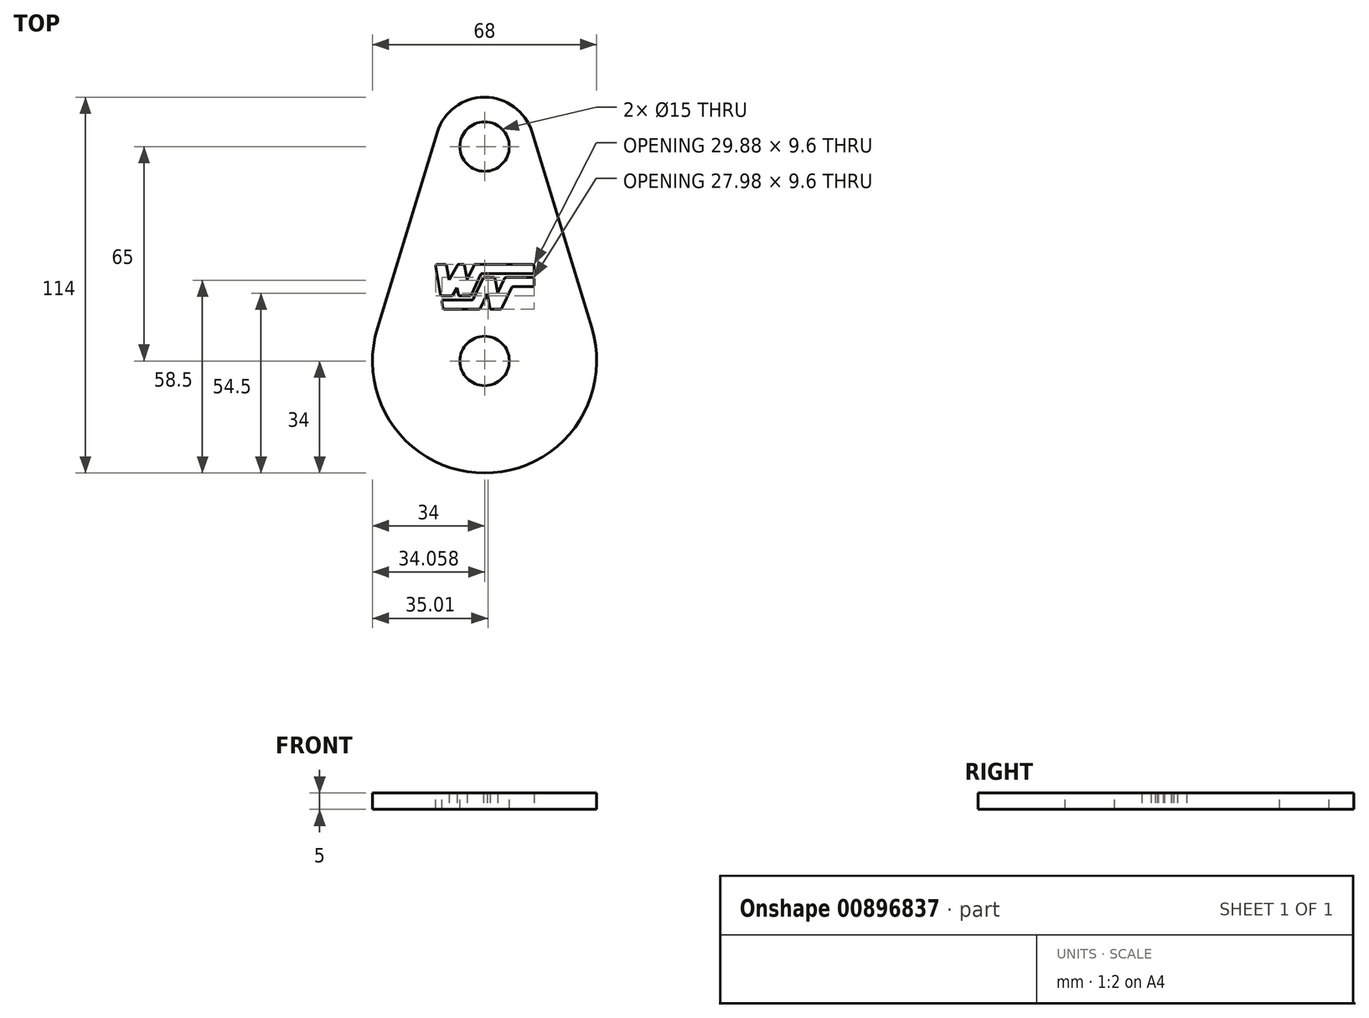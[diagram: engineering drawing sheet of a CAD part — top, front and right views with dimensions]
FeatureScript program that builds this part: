
annotation { "Feature Type Name" : "Feature", "Feature Type Description" : "" }
export const myFeature = defineFeature(function(context is Context, id is Id, definition is map)
    precondition{}
    {
        {
            var Q0;
            Q0=qCreatedBy(makeId("Top.planeOp"),FACE);
            var sketch = newSketch(context, id + "F0", { "sketchPlane" : qUnion([Q0])});
            skArc(sketch, "E0", {"start": v(14.34, 69.38) * mm, "mid": v(0, 80) * mm, "end": v(-14.34, 69.38) * mm});
            skArc(sketch, "E1", {"start": v(-32.52, 9.94) * mm, "mid": v(0, -34) * mm, "end": v(32.52, 9.94) * mm});
            skLineSegment(sketch, "E2", {"start": v(-32.52, 9.94) * mm, "end": v(-14.34, 69.38) * mm});
            skLineSegment(sketch, "E3", {"start": v(14.34, 69.38) * mm, "end": v(32.52, 9.94) * mm});
            skSolve(sketch);
        }
        {
            var Q0;
            Q0=makeQuery(id+"F0.imprint","IMPRINT",FACE,{"disambiguationData":[TD([[makeQuery(id+"F0.imprint","IMPRINT",EDGE,{"derivedFrom":sQuery(id+"F0.wireOp",EDGE,"E0")}),1.0]])]});
            extrude(context, id + "F1", {"entities" : qUnion([Q0]), "flatOperationType" : FlatOperationType.REMOVE, "depth" : 5 * mm, "offsetDistance" : 25 * mm, "domain" : OperationDomain.MODEL});
        }
        {
            var Q0;
            Q0=makeQuery(id+"F1.opExtrude","CAP_FACE",FACE,{"disambiguationData":[OSD([sQuery(id+"F0.wireOp",EDGE,"E0"),sQuery(id+"F0.wireOp",EDGE,"E1"),sQuery(id+"F0.wireOp",EDGE,"E2"),sQuery(id+"F0.wireOp",EDGE,"E3")])],"isStart":true});
            var sketch = newSketch(context, id + "F2", { "sketchPlane" : qUnion([Q0])});
            skPoint(sketch, "E4", {"position": v(0, -65) * mm});
            skPoint(sketch, "E5", {"position": v(0, 0) * mm});
            skSolve(sketch);
        }
        {
            var Q0;
            Q0=sQuery(id+"F2.wireOp",VERTEX,"E4");
            var Q1;
            Q1=sQuery(id+"F2.wireOp",VERTEX,"E5");
            var Q2;
            Q2=makeQuery(id+"F1.opExtrude","SWEPT_BODY",BODY,{"disambiguationData":[OSD([sQuery(id+"F0.wireOp",EDGE,"E0"),sQuery(id+"F0.wireOp",EDGE,"E1"),sQuery(id+"F0.wireOp",EDGE,"E2"),sQuery(id+"F0.wireOp",EDGE,"E3")])]});
            hole(context, id + "F3", {"style" : HoleStyle.SIMPLE, "endStyle" : HoleEndStyle.THROUGH, "holeDiameter" : 15 * mm, "majorDiameter" : 5 * mm, "isTappedThrough" : true, "tappedDepth" : 12 * mm, "tapClearance" : 3, "locations" : qUnion([Q0, Q1]), "scope" : qUnion([Q2])});
        }
        {
            var Q0;
            Q0=qCreatedBy(makeId("Top.planeOp"),FACE);
            var sketch = newSketch(context, id + "F4", { "sketchPlane" : qUnion([Q0])});
            skLineSegment(sketch, "E6.bottom", {"start": v(-15, 15) * mm, "end": v(-15, 30) * mm, "construction": true});
            skLineSegment(sketch, "E6.top", {"start": v(15, 15) * mm, "end": v(15, 30) * mm, "construction": true});
            skLineSegment(sketch, "E6.left", {"start": v(-15, 15) * mm, "end": v(15, 15) * mm, "construction": true});
            skLineSegment(sketch, "E6.right", {"start": v(-15, 30) * mm, "end": v(15, 30) * mm, "construction": true});
            skPoint(sketch, "E6.middle", {"position": v(0, 22.5) * mm});
            skLineSegment(sketch, "E7", {"start": v(15, 22.5) * mm, "end": v(-15, 22.5) * mm, "construction": true});
            skLineSegment(sketch, "E8", {"start": v(-15, 29.3) * mm, "end": v(-13.3, 19.7) * mm});
            skLineSegment(sketch, "E9", {"start": v(-13.3, 19.7) * mm, "end": v(-9.8, 19.7) * mm});
            skLineSegment(sketch, "E10", {"start": v(-9.8, 19.7) * mm, "end": v(-8.36, 22.2) * mm});
            skLineSegment(sketch, "E11", {"start": v(-8.36, 22.2) * mm, "end": v(-7.92, 19.7) * mm});
            skLineSegment(sketch, "E12", {"start": v(-7.92, 19.7) * mm, "end": v(-4.22, 19.7) * mm});
            skLineSegment(sketch, "E13", {"start": v(-4.22, 19.7) * mm, "end": v(-1.05, 26.5) * mm});
            skLineSegment(sketch, "E14", {"start": v(-1.05, 26.5) * mm, "end": v(15, 26.5) * mm});
            skLineSegment(sketch, "E15", {"start": v(15, 26.5) * mm, "end": v(15, 29.3) * mm});
            skLineSegment(sketch, "E16", {"start": v(15, 29.3) * mm, "end": v(-3.17, 29.3) * mm});
            skLineSegment(sketch, "E17", {"start": v(-3.17, 29.3) * mm, "end": v(-5.3, 24.73) * mm});
            skLineSegment(sketch, "E18", {"start": v(-5.3, 24.73) * mm, "end": v(-6.1, 29.3) * mm});
            skLineSegment(sketch, "E19", {"start": v(-6.1, 29.3) * mm, "end": v(-8.1, 29.3) * mm});
            skLineSegment(sketch, "E20", {"start": v(-8.1, 29.3) * mm, "end": v(-10.82, 24.6) * mm});
            skLineSegment(sketch, "E21", {"start": v(-10.82, 24.6) * mm, "end": v(-11.65, 29.3) * mm});
            skLineSegment(sketch, "E22", {"start": v(-11.65, 29.3) * mm, "end": v(-15, 29.3) * mm});
            skLineSegment(sketch, "E23", {"start": v(-13.1, 18.5) * mm, "end": v(-12.6, 15.7) * mm});
            skLineSegment(sketch, "E24", {"start": v(-12.6, 15.7) * mm, "end": v(-1.4, 15.7) * mm});
            skLineSegment(sketch, "E25", {"start": v(-1.4, 15.7) * mm, "end": v(0.79, 20.4) * mm});
            skLineSegment(sketch, "E26", {"start": v(0.79, 20.4) * mm, "end": v(1.62, 15.7) * mm});
            skLineSegment(sketch, "E27", {"start": v(1.62, 15.7) * mm, "end": v(5.12, 15.7) * mm});
            skLineSegment(sketch, "E28", {"start": v(5.12, 15.7) * mm, "end": v(8.29, 22.5) * mm});
            skLineSegment(sketch, "E29", {"start": v(8.29, 22.5) * mm, "end": v(15, 22.5) * mm});
            skLineSegment(sketch, "E30", {"start": v(15, 22.5) * mm, "end": v(15, 25.3) * mm});
            skLineSegment(sketch, "E31", {"start": v(15, 25.3) * mm, "end": v(6.17, 25.3) * mm});
            skLineSegment(sketch, "E32", {"start": v(6.17, 25.3) * mm, "end": v(3.98, 20.6) * mm});
            skLineSegment(sketch, "E33", {"start": v(3.98, 20.6) * mm, "end": v(3.15, 25.3) * mm});
            skLineSegment(sketch, "E34", {"start": v(3.15, 25.3) * mm, "end": v(-0.35, 25.3) * mm});
            skLineSegment(sketch, "E35", {"start": v(-0.35, 25.3) * mm, "end": v(-3.52, 18.5) * mm});
            skLineSegment(sketch, "E36", {"start": v(-3.52, 18.5) * mm, "end": v(-13.1, 18.5) * mm});
            skSolve(sketch);
        }
        {
            var Q0;
            Q0=makeQuery(id+"F1.opExtrude","CAP_FACE",FACE,{"disambiguationData":[OSD([sQuery(id+"F0.wireOp",EDGE,"E0"),sQuery(id+"F0.wireOp",EDGE,"E1"),sQuery(id+"F0.wireOp",EDGE,"E2"),sQuery(id+"F0.wireOp",EDGE,"E3")])],"isStart":false});
            var sketch = newSketch(context, id + "F5", { "sketchPlane" : qUnion([Q0])});
            skLineSegment(sketch, "E37", {"start": v(0, 65) * mm, "end": v(0, 0) * mm, "construction": true});
            skPoint(sketch, "E38", {"position": v(0, 22.5) * mm});
            skSolve(sketch);
        }
        {
            var Q0;
            Q0=sQuery(id+"F5.wireOp",VERTEX,"E38");
            var Q1;
            Q1=qCreatedBy(makeId("Front.planeOp"),FACE);
            cPlane(context, id + "F6", {"entities" : qUnion([Q0, Q1]), "cplaneType" : CPlaneType.PLANE_POINT, "offset" : 0 * mm, "width" : 150 * mm, "height" : 150 * mm});
        }
        {
            var Q0;
            Q0 = qSketchRegion(id + "F4", true);
            extrude(context, id + "F7", {"entities" : qUnion([Q0]), "operationType" : NewBodyOperationType.REMOVE, "endBound" : BoundingType.UP_TO_NEXT, "depth" : 25 * mm, "offsetDistance" : 25 * mm});
        }
        {
            var Q0;
            Q0=makeQuery(id+"F7.boolean.opBoolean","COPY",EDGE,{"derivedFrom":makeQuery(id+"F7.opExtrude","SWEPT_EDGE",EDGE,{"disambiguationData":[OSD([sQuery(id+"F4.wireOp",EDGE,"E21"),sQuery(id+"F4.wireOp",EDGE,"E22")])]})});
            var Q1;
            Q1=makeQuery(id+"F7.boolean.opBoolean","COPY",EDGE,{"derivedFrom":makeQuery(id+"F7.opExtrude","SWEPT_EDGE",EDGE,{"disambiguationData":[OSD([sQuery(id+"F4.wireOp",EDGE,"E8"),sQuery(id+"F4.wireOp",EDGE,"E22")])]})});
            var Q2;
            Q2=makeQuery(id+"F7.boolean.opBoolean","COPY",EDGE,{"derivedFrom":makeQuery(id+"F7.opExtrude","SWEPT_EDGE",EDGE,{"disambiguationData":[OSD([sQuery(id+"F4.wireOp",EDGE,"E19"),sQuery(id+"F4.wireOp",EDGE,"E20")])]})});
            var Q3;
            Q3=makeQuery(id+"F7.boolean.opBoolean","COPY",EDGE,{"derivedFrom":makeQuery(id+"F7.opExtrude","SWEPT_EDGE",EDGE,{"disambiguationData":[OSD([sQuery(id+"F4.wireOp",EDGE,"E8"),sQuery(id+"F4.wireOp",EDGE,"E9")])]})});
            var Q4;
            Q4=makeQuery(id+"F7.boolean.opBoolean","COPY",EDGE,{"derivedFrom":makeQuery(id+"F7.opExtrude","SWEPT_EDGE",EDGE,{"disambiguationData":[OSD([sQuery(id+"F4.wireOp",EDGE,"E11"),sQuery(id+"F4.wireOp",EDGE,"E12")])]})});
            var Q5;
            Q5=makeQuery(id+"F7.boolean.opBoolean","COPY",EDGE,{"derivedFrom":makeQuery(id+"F7.opExtrude","SWEPT_EDGE",EDGE,{"disambiguationData":[OSD([sQuery(id+"F4.wireOp",EDGE,"E12"),sQuery(id+"F4.wireOp",EDGE,"E13")])]})});
            var Q6;
            Q6=makeQuery(id+"F7.boolean.opBoolean","COPY",EDGE,{"derivedFrom":makeQuery(id+"F7.opExtrude","SWEPT_EDGE",EDGE,{"disambiguationData":[OSD([sQuery(id+"F4.wireOp",EDGE,"E13"),sQuery(id+"F4.wireOp",EDGE,"E14")])]})});
            var Q7;
            Q7=makeQuery(id+"F7.boolean.opBoolean","COPY",EDGE,{"derivedFrom":makeQuery(id+"F7.opExtrude","SWEPT_EDGE",EDGE,{"disambiguationData":[OSD([sQuery(id+"F4.wireOp",EDGE,"E9"),sQuery(id+"F4.wireOp",EDGE,"E10")])]})});
            var Q8;
            Q8=makeQuery(id+"F7.boolean.opBoolean","COPY",EDGE,{"derivedFrom":makeQuery(id+"F7.opExtrude","SWEPT_EDGE",EDGE,{"disambiguationData":[OSD([sQuery(id+"F4.wireOp",EDGE,"E18"),sQuery(id+"F4.wireOp",EDGE,"E19")])]})});
            var Q9;
            Q9=makeQuery(id+"F7.boolean.opBoolean","COPY",EDGE,{"derivedFrom":makeQuery(id+"F7.opExtrude","SWEPT_EDGE",EDGE,{"disambiguationData":[OSD([sQuery(id+"F4.wireOp",EDGE,"E16"),sQuery(id+"F4.wireOp",EDGE,"E17")])]})});
            var Q10;
            Q10=makeQuery(id+"F7.boolean.opBoolean","COPY",EDGE,{"derivedFrom":makeQuery(id+"F7.opExtrude","SWEPT_EDGE",EDGE,{"disambiguationData":[OSD([sQuery(id+"F4.wireOp",EDGE,"E15"),sQuery(id+"F4.wireOp",EDGE,"E16")])]})});
            var Q11;
            Q11=makeQuery(id+"F7.boolean.opBoolean","COPY",EDGE,{"derivedFrom":makeQuery(id+"F7.opExtrude","SWEPT_EDGE",EDGE,{"disambiguationData":[OSD([sQuery(id+"F4.wireOp",EDGE,"E14"),sQuery(id+"F4.wireOp",EDGE,"E15")])]})});
            var Q12;
            Q12=makeQuery(id+"F7.boolean.opBoolean","COPY",EDGE,{"derivedFrom":makeQuery(id+"F7.opExtrude","SWEPT_EDGE",EDGE,{"disambiguationData":[OSD([sQuery(id+"F4.wireOp",EDGE,"E29"),sQuery(id+"F4.wireOp",EDGE,"E30")])]})});
            var Q13;
            Q13=makeQuery(id+"F7.boolean.opBoolean","COPY",EDGE,{"derivedFrom":makeQuery(id+"F7.opExtrude","SWEPT_EDGE",EDGE,{"disambiguationData":[OSD([sQuery(id+"F4.wireOp",EDGE,"E28"),sQuery(id+"F4.wireOp",EDGE,"E29")])]})});
            var Q14;
            Q14=makeQuery(id+"F7.boolean.opBoolean","COPY",EDGE,{"derivedFrom":makeQuery(id+"F7.opExtrude","SWEPT_EDGE",EDGE,{"disambiguationData":[OSD([sQuery(id+"F4.wireOp",EDGE,"E27"),sQuery(id+"F4.wireOp",EDGE,"E28")])]})});
            var Q15;
            Q15=makeQuery(id+"F7.boolean.opBoolean","COPY",EDGE,{"derivedFrom":makeQuery(id+"F7.opExtrude","SWEPT_EDGE",EDGE,{"disambiguationData":[OSD([sQuery(id+"F4.wireOp",EDGE,"E24"),sQuery(id+"F4.wireOp",EDGE,"E25")])]})});
            var Q16;
            Q16=makeQuery(id+"F7.boolean.opBoolean","COPY",EDGE,{"derivedFrom":makeQuery(id+"F7.opExtrude","SWEPT_EDGE",EDGE,{"disambiguationData":[OSD([sQuery(id+"F4.wireOp",EDGE,"E33"),sQuery(id+"F4.wireOp",EDGE,"E34")])]})});
            var Q17;
            Q17=makeQuery(id+"F7.boolean.opBoolean","COPY",EDGE,{"derivedFrom":makeQuery(id+"F7.opExtrude","SWEPT_EDGE",EDGE,{"disambiguationData":[OSD([sQuery(id+"F4.wireOp",EDGE,"E35"),sQuery(id+"F4.wireOp",EDGE,"E36")])]})});
            var Q18;
            Q18=makeQuery(id+"F7.boolean.opBoolean","COPY",EDGE,{"derivedFrom":makeQuery(id+"F7.opExtrude","SWEPT_EDGE",EDGE,{"disambiguationData":[OSD([sQuery(id+"F4.wireOp",EDGE,"E23"),sQuery(id+"F4.wireOp",EDGE,"E24")])]})});
            var Q19;
            Q19=makeQuery(id+"F7.boolean.opBoolean","COPY",EDGE,{"derivedFrom":makeQuery(id+"F7.opExtrude","SWEPT_EDGE",EDGE,{"disambiguationData":[OSD([sQuery(id+"F4.wireOp",EDGE,"E23"),sQuery(id+"F4.wireOp",EDGE,"E36")])]})});
            var Q20;
            Q20=makeQuery(id+"F7.boolean.opBoolean","COPY",EDGE,{"derivedFrom":makeQuery(id+"F7.opExtrude","SWEPT_EDGE",EDGE,{"disambiguationData":[OSD([sQuery(id+"F4.wireOp",EDGE,"E31"),sQuery(id+"F4.wireOp",EDGE,"E32")])]})});
            var Q21;
            Q21=makeQuery(id+"F7.boolean.opBoolean","COPY",EDGE,{"derivedFrom":makeQuery(id+"F7.opExtrude","SWEPT_EDGE",EDGE,{"disambiguationData":[OSD([sQuery(id+"F4.wireOp",EDGE,"E30"),sQuery(id+"F4.wireOp",EDGE,"E31")])]})});
            fillet(context, id + "F8", {"entities" : qUnion([Q0, Q1, Q2, Q3, Q4, Q5, Q6, Q7, Q8, Q9, Q10, Q11, Q12, Q13, Q14, Q15, Q16, Q17, Q18, Q19, Q20, Q21]), "radius" : 0.6 * mm, "tangentPropagation" : true, "allowEdgeOverflow" : false});
        }
    });
